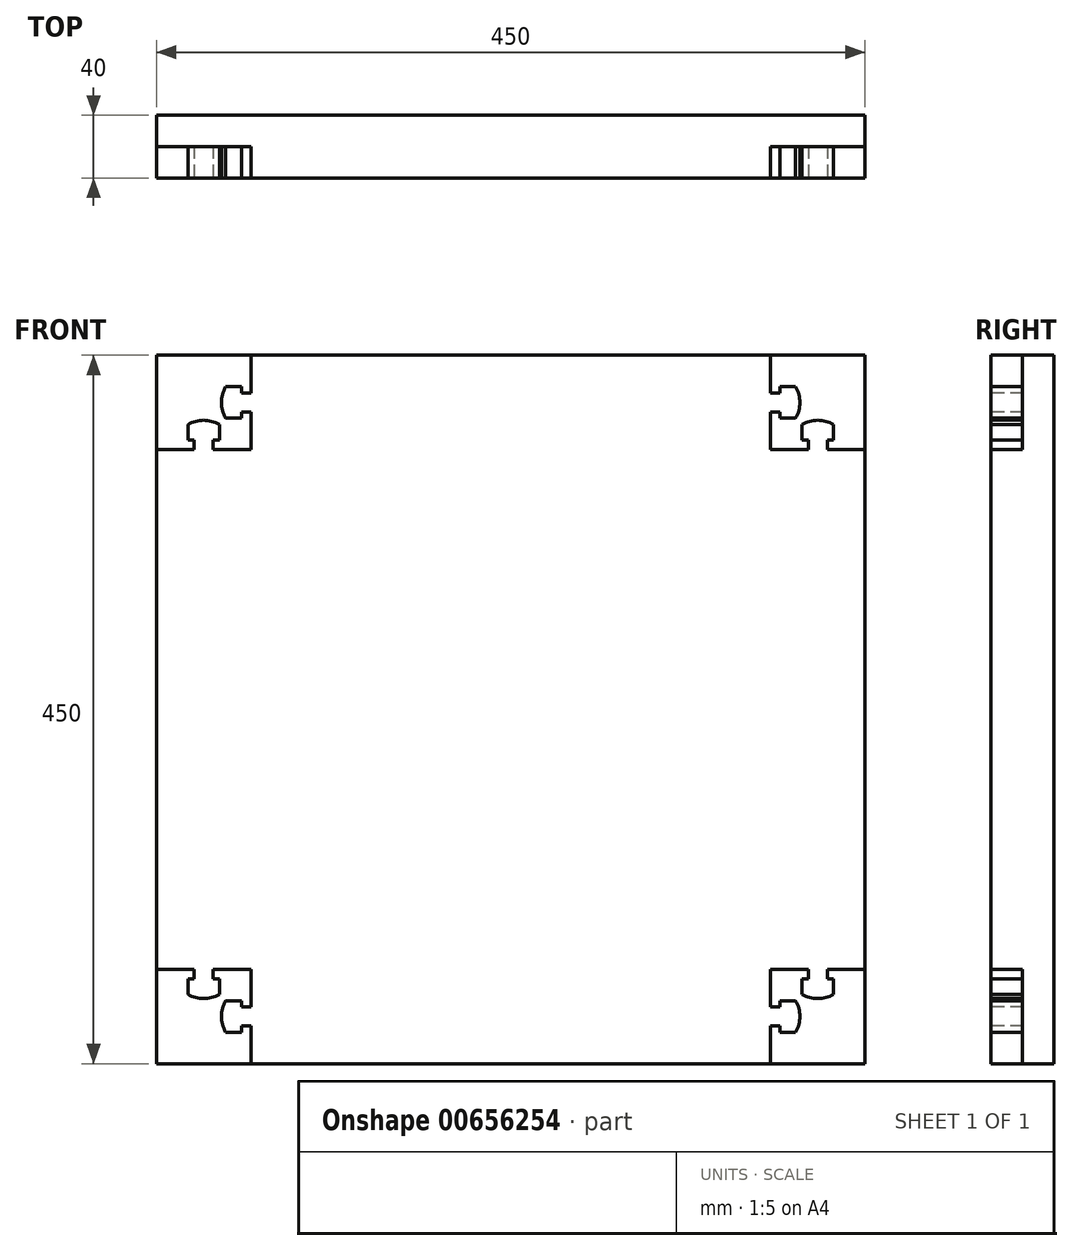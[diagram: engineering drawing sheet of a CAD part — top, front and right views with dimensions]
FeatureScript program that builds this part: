
annotation { "Feature Type Name" : "Feature", "Feature Type Description" : "" }
export const myFeature = defineFeature(function(context is Context, id is Id, definition is map)
    precondition{}
    {
        {
            var Q0;
            Q0=qCreatedBy(makeId("Front.planeOp"),FACE);
            var sketch = newSketch(context, id + "F0", { "sketchPlane" : qUnion([Q0])});
            skLineSegment(sketch, "E0.bottom", {"start": v(225, 225) * mm, "end": v(-225, 225) * mm});
            skLineSegment(sketch, "E0.top", {"start": v(225, -225) * mm, "end": v(-225, -225) * mm});
            skLineSegment(sketch, "E0.left", {"start": v(225, 225) * mm, "end": v(225, -225) * mm});
            skLineSegment(sketch, "E0.right", {"start": v(-225, 225) * mm, "end": v(-225, -225) * mm});
            skPoint(sketch, "E0.middle", {"position": v(0, 0) * mm});
            skLineSegment(sketch, "E1", {"start": v(-225, 165) * mm, "end": v(-165, 165) * mm});
            skLineSegment(sketch, "E2", {"start": v(-165, 165) * mm, "end": v(-165, 225) * mm});
            skLineSegment(sketch, "E3.MirrorCS", {"start": v(-225, -165) * mm, "end": v(-165, -165) * mm});
            skLineSegment(sketch, "E4.MirrorCS", {"start": v(-165, -165) * mm, "end": v(-165, -225) * mm});
            skLineSegment(sketch, "E5.MirrorCS", {"start": v(165, 165) * mm, "end": v(165, 225) * mm});
            skLineSegment(sketch, "E6.MirrorCS", {"start": v(225, 165) * mm, "end": v(165, 165) * mm});
            skLineSegment(sketch, "E7.MirrorCS", {"start": v(225, -165) * mm, "end": v(165, -165) * mm});
            skLineSegment(sketch, "E8.MirrorCS", {"start": v(165, -165) * mm, "end": v(165, -225) * mm});
            skSolve(sketch);
        }
        {
            var Q0;
            {var subQ4=sQuery(id+"F0.wireOp",EDGE,"E1");Q0=makeQuery(id+"F0.imprint","IMPRINT",FACE,{"disambiguationData":[TD([[makeQuery(id+"F0.imprint","IMPRINT",EDGE,{"derivedFrom":subQ4}),-1.0]])]});}
            extrude(context, id + "F1", {"entities" : qUnion([Q0]), "depth" : 40 * mm, "offsetDistance" : 25 * mm});
        }
        {
            var Q0;
            Q0=makeQuery(id+"F1.opExtrude","CAP_FACE",FACE,{"disambiguationData":[OSD([sQuery(id+"F0.wireOp",EDGE,"E0.bottom"),sQuery(id+"F0.wireOp",EDGE,"E0.top"),sQuery(id+"F0.wireOp",EDGE,"E0.left"),sQuery(id+"F0.wireOp",EDGE,"E0.right"),sQuery(id+"F0.wireOp",EDGE,"E1"),sQuery(id+"F0.wireOp",EDGE,"E2"),sQuery(id+"F0.wireOp",EDGE,"E3.MirrorCS"),sQuery(id+"F0.wireOp",EDGE,"E4.MirrorCS"),sQuery(id+"F0.wireOp",EDGE,"E5.MirrorCS"),sQuery(id+"F0.wireOp",EDGE,"E6.MirrorCS"),sQuery(id+"F0.wireOp",EDGE,"E7.MirrorCS"),sQuery(id+"F0.wireOp",EDGE,"E8.MirrorCS")])],"isStart":false});
            var sketch = newSketch(context, id + "F2", { "sketchPlane" : qUnion([Q0])});
            skLineSegment(sketch, "E9", {"start": v(-201, 165) * mm, "end": v(-201, 171) * mm});
            skLineSegment(sketch, "E10", {"start": v(-201, 171) * mm, "end": v(-205, 171) * mm});
            skLineSegment(sketch, "E11", {"start": v(-205, 171) * mm, "end": v(-205, 181) * mm});
            skLineSegment(sketch, "E12", {"start": v(-189, 165) * mm, "end": v(-189, 171) * mm});
            skLineSegment(sketch, "E13", {"start": v(-189, 171) * mm, "end": v(-185, 171) * mm});
            skLineSegment(sketch, "E14", {"start": v(-185, 171) * mm, "end": v(-185, 181) * mm});
            skLineSegment(sketch, "E15", {"start": v(-165, 189) * mm, "end": v(-171, 189) * mm});
            skLineSegment(sketch, "E16", {"start": v(-201, 165) * mm, "end": v(-189, 165) * mm});
            skArc(sketch, "E17", {"start": v(-185, 181) * mm, "mid": v(-195, 183.68) * mm, "end": v(-205, 181) * mm});
            skLineSegment(sketch, "E18", {"start": v(-165, 201) * mm, "end": v(-171, 201) * mm});
            skLineSegment(sketch, "E19", {"start": v(-171, 201) * mm, "end": v(-171, 205) * mm});
            skLineSegment(sketch, "E20", {"start": v(-171, 205) * mm, "end": v(-181, 205) * mm});
            skLineSegment(sketch, "E21", {"start": v(-171, 189) * mm, "end": v(-171, 185) * mm});
            skLineSegment(sketch, "E22", {"start": v(-171, 185) * mm, "end": v(-181, 185) * mm});
            skLineSegment(sketch, "E23", {"start": v(-165, 201) * mm, "end": v(-165, 189) * mm});
            skArc(sketch, "E24", {"start": v(-181, 205) * mm, "mid": v(-183.68, 195) * mm, "end": v(-181, 185) * mm});
            skLineSegment(sketch, "E25.1.0", {"start": v(-185, -171) * mm, "end": v(-185, -181) * mm});
            skArc(sketch, "E25.1.1", {"start": v(-205, -181) * mm, "mid": v(-195, -183.68) * mm, "end": v(-185, -181) * mm});
            skLineSegment(sketch, "E25.1.2", {"start": v(-171, -205) * mm, "end": v(-181, -205) * mm});
            skLineSegment(sketch, "E25.1.3", {"start": v(-171, -185) * mm, "end": v(-181, -185) * mm});
            skArc(sketch, "E25.1.4", {"start": v(-181, -185) * mm, "mid": v(-183.68, -195) * mm, "end": v(-181, -205) * mm});
            skLineSegment(sketch, "E25.1.5", {"start": v(-205, -171) * mm, "end": v(-205, -181) * mm});
            skLineSegment(sketch, "E25.1.6", {"start": v(-201, -165) * mm, "end": v(-189, -165) * mm});
            skLineSegment(sketch, "E25.1.7", {"start": v(-165, -201) * mm, "end": v(-165, -189) * mm});
            skLineSegment(sketch, "E25.1.8", {"start": v(-165, -201) * mm, "end": v(-171, -201) * mm});
            skLineSegment(sketch, "E25.1.9", {"start": v(-171, -201) * mm, "end": v(-171, -205) * mm});
            skLineSegment(sketch, "E25.1.10", {"start": v(-165, -189) * mm, "end": v(-171, -189) * mm});
            skLineSegment(sketch, "E25.1.11", {"start": v(-171, -189) * mm, "end": v(-171, -185) * mm});
            skLineSegment(sketch, "E25.1.12", {"start": v(-189, -165) * mm, "end": v(-189, -171) * mm});
            skLineSegment(sketch, "E25.1.13", {"start": v(-201, -165) * mm, "end": v(-201, -171) * mm});
            skLineSegment(sketch, "E25.1.14", {"start": v(-201, -171) * mm, "end": v(-205, -171) * mm});
            skLineSegment(sketch, "E25.1.15", {"start": v(-189, -171) * mm, "end": v(-185, -171) * mm});
            skLineSegment(sketch, "E25.2.0", {"start": v(171, -185) * mm, "end": v(181, -185) * mm});
            skArc(sketch, "E25.2.1", {"start": v(181, -205) * mm, "mid": v(183.68, -195) * mm, "end": v(181, -185) * mm});
            skLineSegment(sketch, "E25.2.2", {"start": v(205, -171) * mm, "end": v(205, -181) * mm});
            skLineSegment(sketch, "E25.2.3", {"start": v(185, -171) * mm, "end": v(185, -181) * mm});
            skArc(sketch, "E25.2.4", {"start": v(185, -181) * mm, "mid": v(195, -183.68) * mm, "end": v(205, -181) * mm});
            skLineSegment(sketch, "E25.2.5", {"start": v(171, -205) * mm, "end": v(181, -205) * mm});
            skLineSegment(sketch, "E25.2.6", {"start": v(165, -201) * mm, "end": v(165, -189) * mm});
            skLineSegment(sketch, "E25.2.7", {"start": v(201, -165) * mm, "end": v(189, -165) * mm});
            skLineSegment(sketch, "E25.2.8", {"start": v(201, -165) * mm, "end": v(201, -171) * mm});
            skLineSegment(sketch, "E25.2.9", {"start": v(201, -171) * mm, "end": v(205, -171) * mm});
            skLineSegment(sketch, "E25.2.10", {"start": v(189, -165) * mm, "end": v(189, -171) * mm});
            skLineSegment(sketch, "E25.2.11", {"start": v(189, -171) * mm, "end": v(185, -171) * mm});
            skLineSegment(sketch, "E25.2.12", {"start": v(165, -189) * mm, "end": v(171, -189) * mm});
            skLineSegment(sketch, "E25.2.13", {"start": v(165, -201) * mm, "end": v(171, -201) * mm});
            skLineSegment(sketch, "E25.2.14", {"start": v(171, -201) * mm, "end": v(171, -205) * mm});
            skLineSegment(sketch, "E25.2.15", {"start": v(171, -189) * mm, "end": v(171, -185) * mm});
            skLineSegment(sketch, "E25.3.0", {"start": v(185, 171) * mm, "end": v(185, 181) * mm});
            skArc(sketch, "E25.3.1", {"start": v(205, 181) * mm, "mid": v(195, 183.68) * mm, "end": v(185, 181) * mm});
            skLineSegment(sketch, "E25.3.2", {"start": v(171, 205) * mm, "end": v(181, 205) * mm});
            skLineSegment(sketch, "E25.3.3", {"start": v(171, 185) * mm, "end": v(181, 185) * mm});
            skArc(sketch, "E25.3.4", {"start": v(181, 185) * mm, "mid": v(183.68, 195) * mm, "end": v(181, 205) * mm});
            skLineSegment(sketch, "E25.3.5", {"start": v(205, 171) * mm, "end": v(205, 181) * mm});
            skLineSegment(sketch, "E25.3.6", {"start": v(201, 165) * mm, "end": v(189, 165) * mm});
            skLineSegment(sketch, "E25.3.7", {"start": v(165, 201) * mm, "end": v(165, 189) * mm});
            skLineSegment(sketch, "E25.3.8", {"start": v(165, 201) * mm, "end": v(171, 201) * mm});
            skLineSegment(sketch, "E25.3.9", {"start": v(171, 201) * mm, "end": v(171, 205) * mm});
            skLineSegment(sketch, "E25.3.10", {"start": v(165, 189) * mm, "end": v(171, 189) * mm});
            skLineSegment(sketch, "E25.3.11", {"start": v(171, 189) * mm, "end": v(171, 185) * mm});
            skLineSegment(sketch, "E25.3.12", {"start": v(189, 165) * mm, "end": v(189, 171) * mm});
            skLineSegment(sketch, "E25.3.13", {"start": v(201, 165) * mm, "end": v(201, 171) * mm});
            skLineSegment(sketch, "E25.3.14", {"start": v(201, 171) * mm, "end": v(205, 171) * mm});
            skLineSegment(sketch, "E25.3.15", {"start": v(189, 171) * mm, "end": v(185, 171) * mm});
            skPoint(sketch, "E25.center", {"position": v(0, 0) * mm});
            skSolve(sketch);
        }
        {
            var Q0;
            Q0=makeQuery(id+"F2.imprint","IMPRINT",FACE,{"disambiguationData":[TD([[makeQuery(id+"F2.imprint","IMPRINT",EDGE,{"derivedFrom":sQuery(id+"F2.wireOp",EDGE,"E9")}),-1.0]])]});
            var Q1;
            Q1=makeQuery(id+"F2.imprint","IMPRINT",FACE,{"disambiguationData":[TD([[makeQuery(id+"F2.imprint","IMPRINT",EDGE,{"derivedFrom":sQuery(id+"F2.wireOp",EDGE,"E15")}),-1.0]])]});
            var Q2;
            Q2=makeQuery(id+"F2.imprint","IMPRINT",FACE,{"disambiguationData":[TD([[makeQuery(id+"F2.imprint","IMPRINT",EDGE,{"derivedFrom":sQuery(id+"F2.wireOp",EDGE,"E25.3.2")}),-1.0]])]});
            var Q3;
            Q3=makeQuery(id+"F2.imprint","IMPRINT",FACE,{"disambiguationData":[TD([[makeQuery(id+"F2.imprint","IMPRINT",EDGE,{"derivedFrom":sQuery(id+"F2.wireOp",EDGE,"E25.3.0")}),-1.0]])]});
            var Q4;
            Q4=makeQuery(id+"F2.imprint","IMPRINT",FACE,{"disambiguationData":[TD([[makeQuery(id+"F2.imprint","IMPRINT",EDGE,{"derivedFrom":sQuery(id+"F2.wireOp",EDGE,"E25.2.2")}),-1.0]])]});
            var Q5;
            Q5=makeQuery(id+"F2.imprint","IMPRINT",FACE,{"disambiguationData":[TD([[makeQuery(id+"F2.imprint","IMPRINT",EDGE,{"derivedFrom":sQuery(id+"F2.wireOp",EDGE,"E25.2.0")}),-1.0]])]});
            var Q6;
            Q6=makeQuery(id+"F2.imprint","IMPRINT",FACE,{"disambiguationData":[TD([[makeQuery(id+"F2.imprint","IMPRINT",EDGE,{"derivedFrom":sQuery(id+"F2.wireOp",EDGE,"E25.1.2")}),-1.0]])]});
            var Q7;
            Q7=makeQuery(id+"F2.imprint","IMPRINT",FACE,{"disambiguationData":[TD([[makeQuery(id+"F2.imprint","IMPRINT",EDGE,{"derivedFrom":sQuery(id+"F2.wireOp",EDGE,"E25.1.0")}),-1.0]])]});
            var Q8;
            Q8=makeQuery(id+"F1.opExtrude","CAP_FACE",FACE,{"disambiguationData":[OSD([sQuery(id+"F0.wireOp",EDGE,"E0.bottom"),sQuery(id+"F0.wireOp",EDGE,"E0.top"),sQuery(id+"F0.wireOp",EDGE,"E0.left"),sQuery(id+"F0.wireOp",EDGE,"E0.right"),sQuery(id+"F0.wireOp",EDGE,"E1"),sQuery(id+"F0.wireOp",EDGE,"E2"),sQuery(id+"F0.wireOp",EDGE,"E3.MirrorCS"),sQuery(id+"F0.wireOp",EDGE,"E4.MirrorCS"),sQuery(id+"F0.wireOp",EDGE,"E5.MirrorCS"),sQuery(id+"F0.wireOp",EDGE,"E6.MirrorCS"),sQuery(id+"F0.wireOp",EDGE,"E7.MirrorCS"),sQuery(id+"F0.wireOp",EDGE,"E8.MirrorCS")])],"isStart":true});
            extrude(context, id + "F3", {"entities" : qUnion([Q0, Q1, Q2, Q3, Q4, Q5, Q6, Q7]), "operationType" : NewBodyOperationType.ADD, "endBound" : BoundingType.UP_TO_SURFACE, "oppositeDirection" : true, "depth" : 25 * mm, "endBoundEntityFace" : qUnion([Q8]), "offsetDistance" : 25 * mm});
        }
        {
            var Q0;
            {var subQ0=sQuery(id+"F0.wireOp",EDGE,"E8.MirrorCS");var subQ1=sQuery(id+"F0.wireOp",EDGE,"E7.MirrorCS");var subQ2=sQuery(id+"F0.wireOp",EDGE,"E6.MirrorCS");var subQ3=sQuery(id+"F0.wireOp",EDGE,"E5.MirrorCS");var subQ4=sQuery(id+"F0.wireOp",EDGE,"E4.MirrorCS");var subQ5=sQuery(id+"F0.wireOp",EDGE,"E3.MirrorCS");var subQ6=sQuery(id+"F0.wireOp",EDGE,"E2");var subQ7=sQuery(id+"F0.wireOp",EDGE,"E1");var subQ8=sQuery(id+"F0.wireOp",EDGE,"E0.right");var subQ9=sQuery(id+"F0.wireOp",EDGE,"E0.left");var subQ10=sQuery(id+"F0.wireOp",EDGE,"E0.top");var subQ11=sQuery(id+"F0.wireOp",EDGE,"E0.bottom");Q0=makeQuery(id+"F3.boolean.opBoolean","MERGE",FACE,{"derivedFrom":[makeQuery(id+"F1.opExtrude","CAP_FACE",FACE,{"disambiguationData":[OSD([subQ11,subQ10,subQ9,subQ8,subQ7,subQ6,subQ5,subQ4,subQ3,subQ2,subQ1,subQ0])],"isStart":true}),makeQuery(id+"F3.opExtrude","CAP_FACE",FACE,{"disambiguationData":[OSD([subQ11,subQ10,subQ9,subQ8,subQ7,subQ6,subQ5,subQ4,subQ3,subQ2,subQ1,subQ0]),OD(0.0)],"isStart":false}),makeQuery(id+"F3.opExtrude","CAP_FACE",FACE,{"disambiguationData":[OSD([subQ11,subQ10,subQ9,subQ8,subQ7,subQ6,subQ5,subQ4,subQ3,subQ2,subQ1,subQ0]),OD(1.0)],"isStart":false}),makeQuery(id+"F3.opExtrude","CAP_FACE",FACE,{"disambiguationData":[OSD([subQ11,subQ10,subQ9,subQ8,subQ7,subQ6,subQ5,subQ4,subQ3,subQ2,subQ1,subQ0]),OD(2.0)],"isStart":false}),makeQuery(id+"F3.opExtrude","CAP_FACE",FACE,{"disambiguationData":[OSD([subQ11,subQ10,subQ9,subQ8,subQ7,subQ6,subQ5,subQ4,subQ3,subQ2,subQ1,subQ0]),OD(3.0)],"isStart":false}),makeQuery(id+"F3.opExtrude","CAP_FACE",FACE,{"disambiguationData":[OSD([subQ11,subQ10,subQ9,subQ8,subQ7,subQ6,subQ5,subQ4,subQ3,subQ2,subQ1,subQ0]),OD(4.0)],"isStart":false}),makeQuery(id+"F3.opExtrude","CAP_FACE",FACE,{"disambiguationData":[OSD([subQ11,subQ10,subQ9,subQ8,subQ7,subQ6,subQ5,subQ4,subQ3,subQ2,subQ1,subQ0]),OD(5.0)],"isStart":false}),makeQuery(id+"F3.opExtrude","CAP_FACE",FACE,{"disambiguationData":[OSD([subQ11,subQ10,subQ9,subQ8,subQ7,subQ6,subQ5,subQ4,subQ3,subQ2,subQ1,subQ0]),OD(6.0)],"isStart":false}),makeQuery(id+"F3.opExtrude","CAP_FACE",FACE,{"disambiguationData":[OSD([subQ11,subQ10,subQ9,subQ8,subQ7,subQ6,subQ5,subQ4,subQ3,subQ2,subQ1,subQ0]),OD(7.0)],"isStart":false})]});}
            var sketch = newSketch(context, id + "F4", { "sketchPlane" : qUnion([Q0])});
            skLineSegment(sketch, "E26.bottom", {"start": v(225, 225) * mm, "end": v(-225, 225) * mm});
            skLineSegment(sketch, "E26.top", {"start": v(225, -225) * mm, "end": v(-225, -225) * mm});
            skLineSegment(sketch, "E26.left", {"start": v(225, 225) * mm, "end": v(225, -225) * mm});
            skLineSegment(sketch, "E26.right", {"start": v(-225, 225) * mm, "end": v(-225, -225) * mm});
            skPoint(sketch, "E26.middle", {"position": v(0, 0) * mm});
            skLineSegment(sketch, "E27", {"start": v(-225, 165) * mm, "end": v(-165, 165) * mm});
            skLineSegment(sketch, "E28", {"start": v(-165, 165) * mm, "end": v(-165, 225) * mm});
            skLineSegment(sketch, "E29.MirrorCS", {"start": v(-225, -165) * mm, "end": v(-165, -165) * mm});
            skLineSegment(sketch, "E30.MirrorCS", {"start": v(-165, -165) * mm, "end": v(-165, -225) * mm});
            skLineSegment(sketch, "E31.MirrorCS", {"start": v(165, 165) * mm, "end": v(165, 225) * mm});
            skLineSegment(sketch, "E32.MirrorCS", {"start": v(225, 165) * mm, "end": v(165, 165) * mm});
            skLineSegment(sketch, "E33.MirrorCS", {"start": v(225, -165) * mm, "end": v(165, -165) * mm});
            skLineSegment(sketch, "E34.MirrorCS", {"start": v(165, -165) * mm, "end": v(165, -225) * mm});
            skSolve(sketch);
        }
        {
            var Q0;
            {var subQ4=sQuery(id+"F4.wireOp",EDGE,"E31.MirrorCS");var subQ6=sQuery(id+"F4.wireOp",EDGE,"E26.bottom");var subQ7=makeQuery(id+"F4.imprint","INTERSECT",VERTEX,{"derivedFrom":[subQ6,subQ4]});var subQ29=sQuery(id+"F4.wireOp",EDGE,"E28");var subQ32=makeQuery(id+"F4.imprint","INTERSECT",VERTEX,{"derivedFrom":[subQ6,subQ29]});Q0=makeQuery(id+"F4.imprint","IMPRINT",FACE,{"disambiguationData":[TD([[makeQuery(id+"F4.imprint","IMPRINT",EDGE,{"disambiguationData":[TD([[subQ7,1.0],[subQ32,-1.0]])],"derivedFrom":subQ6}),-1.0]])]});}
            var Q1;
            {var subQ2=sQuery(id+"F4.wireOp",EDGE,"E26.left");var subQ5=sQuery(id+"F4.wireOp",EDGE,"E34.MirrorCS");var subQ6=sQuery(id+"F4.wireOp",EDGE,"E26.top");var subQ7=makeQuery(id+"F4.imprint","INTERSECT",VERTEX,{"derivedFrom":[subQ6,subQ5]});var subQ11=makeQuery(id+"F4.imprint","INTERSECT",VERTEX,{"derivedFrom":[subQ6,subQ2]});Q1=makeQuery(id+"F4.imprint","IMPRINT",FACE,{"disambiguationData":[TD([[makeQuery(id+"F4.imprint","IMPRINT",EDGE,{"disambiguationData":[TD([[subQ7,1.0],[subQ11,-1.0]])],"derivedFrom":subQ6}),-1.0]])]});}
            var Q2;
            {var subQ1=sQuery(id+"F4.wireOp",EDGE,"E30.MirrorCS");var subQ5=sQuery(id+"F4.wireOp",EDGE,"E26.top");var subQ6=makeQuery(id+"F4.imprint","INTERSECT",VERTEX,{"derivedFrom":[subQ5,subQ1]});var subQ8=sQuery(id+"F4.wireOp",EDGE,"E26.right");var subQ9=makeQuery(id+"F4.imprint","INTERSECT",VERTEX,{"derivedFrom":[subQ5,subQ8]});Q2=makeQuery(id+"F4.imprint","IMPRINT",FACE,{"disambiguationData":[TD([[makeQuery(id+"F4.imprint","IMPRINT",EDGE,{"disambiguationData":[TD([[subQ6,-1.0],[subQ9,1.0]])],"derivedFrom":subQ5}),-1.0]])]});}
            var Q3;
            {var subQ2=sQuery(id+"F4.wireOp",EDGE,"E26.right");var subQ4=sQuery(id+"F4.wireOp",EDGE,"E26.bottom");var subQ5=makeQuery(id+"F4.imprint","INTERSECT",VERTEX,{"derivedFrom":[subQ4,subQ2]});var subQ6=sQuery(id+"F4.wireOp",EDGE,"E28");var subQ7=makeQuery(id+"F4.imprint","INTERSECT",VERTEX,{"derivedFrom":[subQ4,subQ6]});Q3=makeQuery(id+"F4.imprint","IMPRINT",FACE,{"disambiguationData":[TD([[makeQuery(id+"F4.imprint","IMPRINT",EDGE,{"disambiguationData":[TD([[subQ7,-1.0],[subQ5,1.0]])],"derivedFrom":subQ4}),1.0]])]});}
            var Q4;
            {var subQ3=sQuery(id+"F4.wireOp",EDGE,"E26.left");var subQ5=sQuery(id+"F4.wireOp",EDGE,"E31.MirrorCS");var subQ6=sQuery(id+"F4.wireOp",EDGE,"E26.bottom");var subQ7=makeQuery(id+"F4.imprint","INTERSECT",VERTEX,{"derivedFrom":[subQ6,subQ5]});var subQ8=makeQuery(id+"F4.imprint","INTERSECT",VERTEX,{"derivedFrom":[subQ6,subQ3]});Q4=makeQuery(id+"F4.imprint","IMPRINT",FACE,{"disambiguationData":[TD([[makeQuery(id+"F4.imprint","IMPRINT",EDGE,{"disambiguationData":[TD([[subQ7,1.0],[subQ8,-1.0]])],"derivedFrom":subQ6}),1.0]])]});}
            extrude(context, id + "F5", {"entities" : qUnion([Q0, Q1, Q2, Q3, Q4]), "operationType" : NewBodyOperationType.ADD, "oppositeDirection" : true, "depth" : 20 * mm, "offsetDistance" : 25 * mm});
        }
    });
